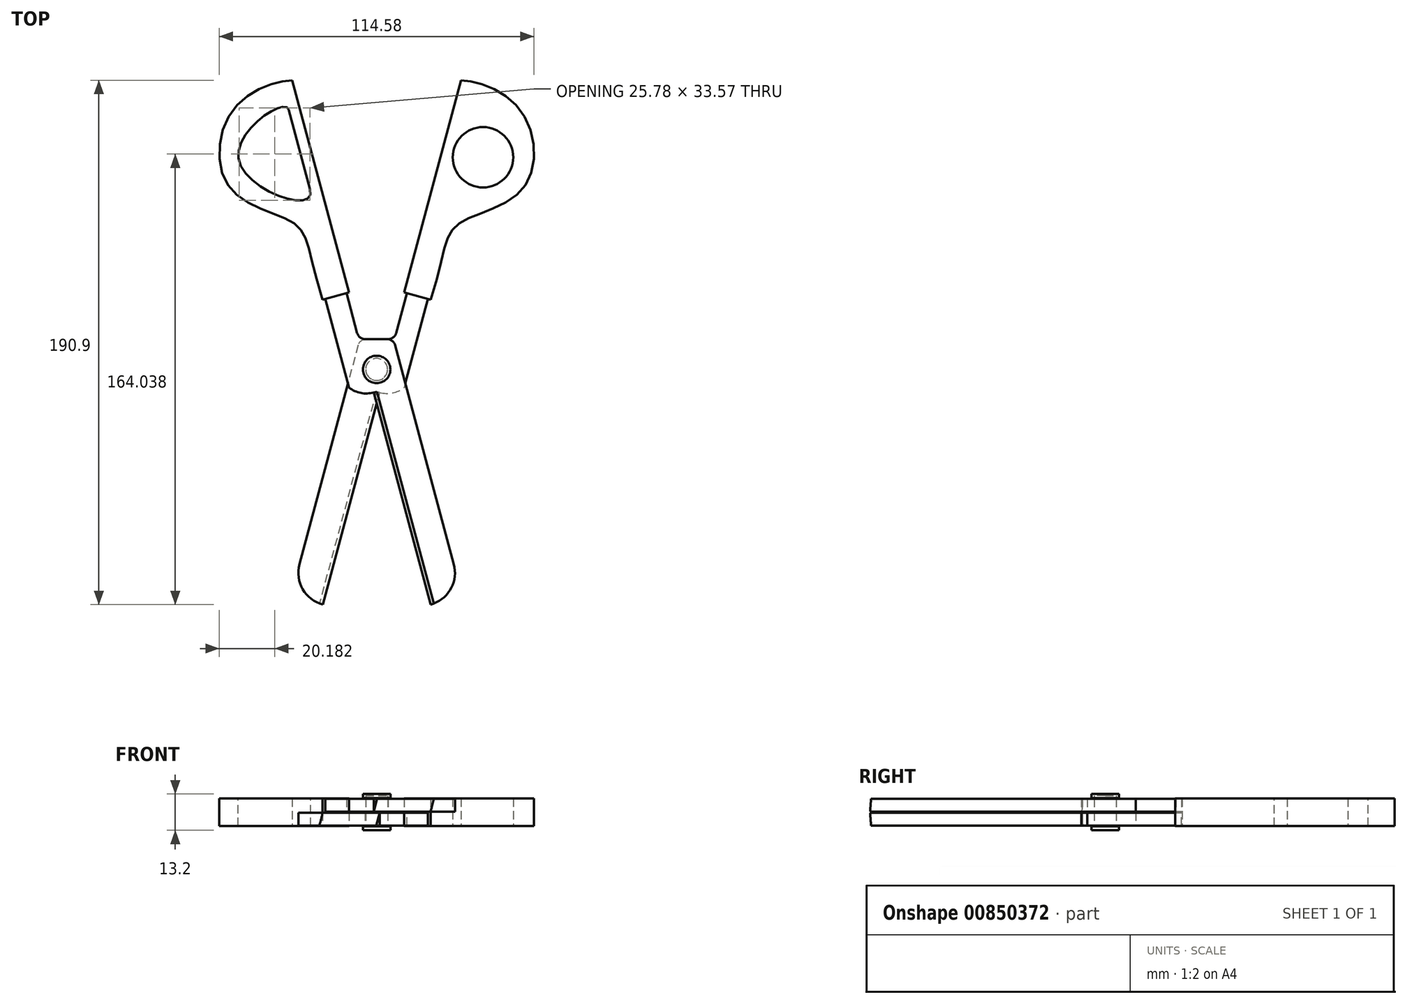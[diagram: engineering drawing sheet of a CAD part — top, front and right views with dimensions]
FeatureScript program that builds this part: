
annotation { "Feature Type Name" : "Feature", "Feature Type Description" : "" }
export const myFeature = defineFeature(function(context is Context, id is Id, definition is map)
    precondition{}
    {
        {
            var Q0;
            Q0=qCreatedBy(makeId("Top.planeOp"),FACE);
            var sketch = newSketch(context, id + "F0", { "sketchPlane" : qUnion([Q0])});
            skLineSegment(sketch, "E0", {"start": v(10, 10) * mm, "end": v(30.7, 87.27) * mm});
            skLineSegment(sketch, "E1", {"start": v(10, 10) * mm, "end": v(19.66, 7.41) * mm});
            skFitSpline(sketch, "E2", {"points": [v(19.66, 7.41) * mm, v(30.07, 35.15) * mm, v(53.27, 47.9) * mm, v(52.13, 76.77) * mm, v(30.7, 87.27) * mm], "startDerivative": vector(62.66, 194.88) * mm, "endDerivative": vector(-72.65, 2.28) * mm});
            skLineSegment(sketch, "E3.MirrorCS", {"start": v(-10, 10) * mm, "end": v(-30.7, 87.27) * mm});
            skFitSpline(sketch, "E4.MirrorCS", {"points": [v(-19.66, 7.41) * mm, v(-30.07, 35.15) * mm, v(-53.27, 47.9) * mm, v(-52.13, 76.77) * mm, v(-30.7, 87.27) * mm], "startDerivative": vector(-62.66, 194.88) * mm, "endDerivative": vector(72.65, 2.28) * mm});
            skLineSegment(sketch, "E5.MirrorCS", {"start": v(-10, 10) * mm, "end": v(-19.66, 7.41) * mm});
            skSolve(sketch);
        }
        {
            var Q0;
            Q0=qSketchRegion(id+"F0",true);
            extrude(context, id + "F1", {"entities" : qUnion([Q0]), "endBound" : BoundingType.SYMMETRIC, "depth" : 10 * mm, "offsetDistance" : 25 * mm});
        }
        {
            var Q0;
            Q0=qCreatedBy(makeId("Top.planeOp"),FACE);
            var sketch = newSketch(context, id + "F2", { "sketchPlane" : qUnion([Q0])});
            skLineSegment(sketch, "E6", {"start": v(-31.98, 76.58) * mm, "end": v(-24.22, 47.6) * mm});
            skFitSpline(sketch, "E7", {"points": [v(-31.98, 76.58) * mm, v(-50.17, 58.1) * mm, v(-24.22, 47.6) * mm], "startDerivative": vector(-7.92, 29.54) * mm, "endDerivative": vector(-15.24, 56.87) * mm});
            skSolve(sketch);
        }
        {
            var Q0;
            Q0=qSketchRegion(id+"F2",true);
            extrude(context, id + "F3", {"entities" : qUnion([Q0]), "operationType" : NewBodyOperationType.REMOVE, "endBound" : BoundingType.SYMMETRIC, "oppositeDirection" : true, "depth" : 40 * mm, "offsetDistance" : 25 * mm});
        }
        {
            var Q0;
            Q0=qCreatedBy(makeId("Top.planeOp"),FACE);
            var sketch = newSketch(context, id + "F4", { "sketchPlane" : qUnion([Q0])});
            skCircle(sketch, "E8", {"center": v(38.72, 59.24) * mm, "radius": 11 * mm});
            skSolve(sketch);
        }
        {
            var Q0;
            Q0=qSketchRegion(id+"F4",true);
            extrude(context, id + "F5", {"entities" : qUnion([Q0]), "operationType" : NewBodyOperationType.REMOVE, "endBound" : BoundingType.SYMMETRIC, "depth" : 40 * mm, "offsetDistance" : 25 * mm});
        }
        {
            var Q0;
            Q0=qCreatedBy(makeId("Top.planeOp"),FACE);
            var sketch = newSketch(context, id + "F6", { "sketchPlane" : qUnion([Q0])});
            skCircle(sketch, "E9", {"center": v(0, -18) * mm, "radius": 4 * mm});
            skSolve(sketch);
        }
        {
            var Q0;
            Q0=qSketchRegion(id+"F6",true);
            extrude(context, id + "F7", {"entities" : qUnion([Q0]), "endBound" : BoundingType.SYMMETRIC, "depth" : 12 * mm, "offsetDistance" : 25 * mm});
        }
        {
            var Q0;
            Q0=qCreatedBy(makeId("Top.planeOp"),FACE);
            cPlane(context, id + "F8", {"entities" : qUnion([Q0]), "cplaneType" : CPlaneType.OFFSET, "offset" : 2.5 * mm, "width" : 150 * mm, "height" : 150 * mm});
        }
        {
            var Q0;
            Q0=qCreatedBy(id+"F8.planeOp",FACE);
            var sketch = newSketch(context, id + "F9", { "sketchPlane" : qUnion([Q0])});
            skLineSegment(sketch, "E10", {"start": v(-19.99, 12.5) * mm, "end": v(-14.81, -6.82) * mm});
            skLineSegment(sketch, "E11", {"start": v(-12.26, 14.57) * mm, "end": v(-7.08, -4.75) * mm});
            skArc(sketch, "E12", {"start": v(-7.08, -4.75) * mm, "mid": v(-6.01, -6.35) * mm, "end": v(-4.19, -6.97) * mm});
            skLineSegment(sketch, "E13", {"start": v(-4.19, -6.97) * mm, "end": v(0, -6.97) * mm});
            skLineSegment(sketch, "E14.MirrorCS", {"start": v(4.19, -6.97) * mm, "end": v(0, -6.97) * mm});
            skArc(sketch, "E15", {"start": v(4.19, -6.97) * mm, "mid": v(5.8, -7.68) * mm, "end": v(6.73, -9.17) * mm});
            skLineSegment(sketch, "E16", {"start": v(6.73, -9.17) * mm, "end": v(28.1, -88.93) * mm});
            skLineSegment(sketch, "E17", {"start": v(-14.81, -6.82) * mm, "end": v(-10.04, -24.61) * mm});
            skArc(sketch, "E18", {"start": v(-10.04, -24.61) * mm, "mid": v(-5.78, -26.56) * mm, "end": v(-1.1, -26.35) * mm});
            skLineSegment(sketch, "E19", {"start": v(-1.1, -26.35) * mm, "end": v(19.61, -103.63) * mm});
            skArc(sketch, "E20", {"start": v(19.61, -103.63) * mm, "mid": v(26.9, -98.04) * mm, "end": v(28.1, -88.93) * mm});
            skLineSegment(sketch, "E21", {"start": v(-19.99, 12.5) * mm, "end": v(-12.26, 14.57) * mm});
            skSolve(sketch);
        }
        {
            var Q0;
            Q0=qSketchRegion(id+"F9",true);
            extrude(context, id + "F10", {"entities" : qUnion([Q0]), "endBound" : BoundingType.SYMMETRIC, "depth" : 4.7 * mm, "offsetDistance" : 25 * mm});
        }
        {
            var Q0;
            Q0=qCreatedBy(makeId("Top.planeOp"),FACE);
            cPlane(context, id + "F11", {"entities" : qUnion([Q0]), "cplaneType" : CPlaneType.OFFSET, "offset" : 2.5 * mm, "oppositeDirection" : true, "width" : 150 * mm, "height" : 150 * mm});
        }
        {
            var Q0;
            Q0=qCreatedBy(id+"F11.planeOp",FACE);
            var sketch = newSketch(context, id + "F12", { "sketchPlane" : qUnion([Q0])});
            skLineSegment(sketch, "E22", {"start": v(12.26, 14.57) * mm, "end": v(7.08, -4.75) * mm});
            skLineSegment(sketch, "E23", {"start": v(19.99, 12.5) * mm, "end": v(14.81, -6.82) * mm});
            skArc(sketch, "E24", {"start": v(7.08, -4.75) * mm, "mid": v(6.01, -6.35) * mm, "end": v(4.19, -6.97) * mm});
            skLineSegment(sketch, "E25", {"start": v(4.19, -6.97) * mm, "end": v(0, -6.97) * mm});
            skLineSegment(sketch, "E26.MirrorCS", {"start": v(-4.19, -6.97) * mm, "end": v(0, -6.97) * mm});
            skArc(sketch, "E27", {"start": v(-4.19, -6.97) * mm, "mid": v(-5.8, -7.68) * mm, "end": v(-6.73, -9.17) * mm});
            skLineSegment(sketch, "E28", {"start": v(-6.73, -9.17) * mm, "end": v(-28.1, -88.93) * mm});
            skLineSegment(sketch, "E29", {"start": v(14.81, -6.82) * mm, "end": v(10.04, -24.61) * mm});
            skArc(sketch, "E30", {"start": v(10.04, -24.61) * mm, "mid": v(5.78, -26.56) * mm, "end": v(1.1, -26.35) * mm});
            skLineSegment(sketch, "E31", {"start": v(1.1, -26.35) * mm, "end": v(-19.61, -103.63) * mm});
            skArc(sketch, "E32", {"start": v(-28.1, -88.93) * mm, "mid": v(-26.9, -98.04) * mm, "end": v(-19.61, -103.63) * mm});
            skLineSegment(sketch, "E33", {"start": v(12.26, 14.57) * mm, "end": v(19.99, 12.5) * mm});
            skSolve(sketch);
        }
        {
            var Q0;
            Q0=makeQuery(id+"F10.opExtrude","SWEPT_FACE",FACE,{"disambiguationData":[OSD([sQuery(id+"F9.wireOp",EDGE,"E21")])]});
            cPlane(context, id + "F13", {"entities" : qUnion([Q0]), "cplaneType" : CPlaneType.OFFSET, "offset" : 122.5 * mm, "oppositeDirection" : true, "width" : 150 * mm, "height" : 150 * mm});
        }
        {
            var Q0;
            Q0=qCreatedBy(id+"F13.planeOp",FACE);
            var sketch = newSketch(context, id + "F14", { "sketchPlane" : qUnion([Q0])});
            skLineSegment(sketch, "E34", {"start": v(7.88, 0.15) * mm, "end": v(6.62, 4.85) * mm});
            skLineSegment(sketch, "E35", {"start": v(6.62, 4.85) * mm, "end": v(7.88, 4.85) * mm});
            skLineSegment(sketch, "E36", {"start": v(7.88, 4.85) * mm, "end": v(7.88, 0.15) * mm});
            skSolve(sketch);
        }
        {
            var Q0;
            Q0=qSketchRegion(id+"F14",true);
            extrude(context, id + "F15", {"entities" : qUnion([Q0]), "operationType" : NewBodyOperationType.REMOVE, "depth" : 80 * mm, "offsetDistance" : 25 * mm});
        }
        {
            var Q0;
            Q0=qSketchRegion(id+"F12",true);
            extrude(context, id + "F16", {"entities" : qUnion([Q0]), "endBound" : BoundingType.SYMMETRIC, "depth" : 4.7 * mm, "offsetDistance" : 25 * mm});
        }
        {
            var Q0;
            Q0=makeQuery(id+"F10.opExtrude","CAP_FACE",FACE,{"disambiguationData":[OSD([sQuery(id+"F9.wireOp",EDGE,"E10"),sQuery(id+"F9.wireOp",EDGE,"E11"),sQuery(id+"F9.wireOp",EDGE,"E12"),sQuery(id+"F9.wireOp",EDGE,"E13"),sQuery(id+"F9.wireOp",EDGE,"E14.MirrorCS"),sQuery(id+"F9.wireOp",EDGE,"E15"),sQuery(id+"F9.wireOp",EDGE,"E16"),sQuery(id+"F9.wireOp",EDGE,"E17"),sQuery(id+"F9.wireOp",EDGE,"E18"),sQuery(id+"F9.wireOp",EDGE,"E19"),sQuery(id+"F9.wireOp",EDGE,"E20"),sQuery(id+"F9.wireOp",EDGE,"E21")])],"isStart":false});
            cPlane(context, id + "F17", {"entities" : qUnion([Q0]), "cplaneType" : CPlaneType.OFFSET, "offset" : 1 * mm, "width" : 150 * mm, "height" : 150 * mm});
        }
        {
            var Q0;
            Q0=qCreatedBy(id+"F17.planeOp",FACE);
            var sketch = newSketch(context, id + "F18", { "sketchPlane" : qUnion([Q0])});
            skCircle(sketch, "E37", {"center": v(0, -18) * mm, "radius": 5 * mm});
            skSolve(sketch);
        }
        {
            var Q0;
            Q0=qSketchRegion(id+"F18",true);
            extrude(context, id + "F19", {"entities" : qUnion([Q0]), "endBound" : BoundingType.SYMMETRIC, "depth" : 1.5 * mm, "offsetDistance" : 25 * mm});
        }
        {
            var Q0;
            Q0=makeQuery(id+"F16.opExtrude","SWEPT_FACE",FACE,{"disambiguationData":[OSD([sQuery(id+"F12.wireOp",EDGE,"E33")])]});
            cPlane(context, id + "F20", {"entities" : qUnion([Q0]), "cplaneType" : CPlaneType.OFFSET, "offset" : 122.5 * mm, "oppositeDirection" : true, "width" : 150 * mm, "height" : 150 * mm});
        }
        {
            var Q0;
            Q0=qCreatedBy(id+"F20.planeOp",FACE);
            var sketch = newSketch(context, id + "F21", { "sketchPlane" : qUnion([Q0])});
            skLineSegment(sketch, "E38", {"start": v(-7.88, -0.15) * mm, "end": v(-7.88, -4.85) * mm});
            skLineSegment(sketch, "E39", {"start": v(-7.88, -4.85) * mm, "end": v(-6.62, -4.85) * mm});
            skLineSegment(sketch, "E40", {"start": v(-6.62, -4.85) * mm, "end": v(-7.88, -0.15) * mm});
            skSolve(sketch);
        }
        {
            var Q0;
            Q0=qSketchRegion(id+"F21",true);
            extrude(context, id + "F22", {"entities" : qUnion([Q0]), "operationType" : NewBodyOperationType.REMOVE, "depth" : 80 * mm, "offsetDistance" : 25 * mm});
        }
        {
            var Q0;
            Q0=makeQuery(id+"F16.opExtrude","CAP_FACE",FACE,{"disambiguationData":[OSD([sQuery(id+"F12.wireOp",EDGE,"E22"),sQuery(id+"F12.wireOp",EDGE,"E23"),sQuery(id+"F12.wireOp",EDGE,"E24"),sQuery(id+"F12.wireOp",EDGE,"E25"),sQuery(id+"F12.wireOp",EDGE,"E26.MirrorCS"),sQuery(id+"F12.wireOp",EDGE,"E27"),sQuery(id+"F12.wireOp",EDGE,"E28"),sQuery(id+"F12.wireOp",EDGE,"E29"),sQuery(id+"F12.wireOp",EDGE,"E30"),sQuery(id+"F12.wireOp",EDGE,"E31"),sQuery(id+"F12.wireOp",EDGE,"E32"),sQuery(id+"F12.wireOp",EDGE,"E33")])],"isStart":true});
            cPlane(context, id + "F23", {"entities" : qUnion([Q0]), "cplaneType" : CPlaneType.OFFSET, "offset" : 1 * mm, "width" : 150 * mm, "height" : 150 * mm});
        }
        {
            var Q0;
            Q0=qCreatedBy(id+"F23.planeOp",FACE);
            var sketch = newSketch(context, id + "F24", { "sketchPlane" : qUnion([Q0])});
            skCircle(sketch, "E41", {"center": v(0, 18) * mm, "radius": 5 * mm});
            skSolve(sketch);
        }
        {
            var Q0;
            Q0=qSketchRegion(id+"F24",true);
            extrude(context, id + "F25", {"entities" : qUnion([Q0]), "operationType" : NewBodyOperationType.ADD, "endBound" : BoundingType.SYMMETRIC, "depth" : 1.5 * mm, "offsetDistance" : 25 * mm});
        }
        {
            var Q0;
            Q0=makeQuery(id+"F1.opExtrude","SWEPT_BODY",BODY,{"disambiguationData":[OSD([sQuery(id+"F0.wireOp",EDGE,"E0"),sQuery(id+"F0.wireOp",EDGE,"E1"),sQuery(id+"F0.wireOp",EDGE,"E2")])]});
            var Q1;
            Q1=makeQuery(id+"F16.opExtrude","SWEPT_BODY",BODY,{"disambiguationData":[OSD([sQuery(id+"F12.wireOp",EDGE,"E22"),sQuery(id+"F12.wireOp",EDGE,"E23"),sQuery(id+"F12.wireOp",EDGE,"E24"),sQuery(id+"F12.wireOp",EDGE,"E25"),sQuery(id+"F12.wireOp",EDGE,"E26.MirrorCS"),sQuery(id+"F12.wireOp",EDGE,"E27"),sQuery(id+"F12.wireOp",EDGE,"E28"),sQuery(id+"F12.wireOp",EDGE,"E29"),sQuery(id+"F12.wireOp",EDGE,"E30"),sQuery(id+"F12.wireOp",EDGE,"E31"),sQuery(id+"F12.wireOp",EDGE,"E32"),sQuery(id+"F12.wireOp",EDGE,"E33")])]});
            booleanBodies(context, id + "F26", {"operationType" : BooleanOperationType.SUBTRACTION, "tools" : qUnion([Q0]), "targets" : qUnion([Q1]), "keepTools" : true});
        }
        {
            var Q0;
            Q0=makeQuery(id+"F1.opExtrude","SWEPT_BODY",BODY,{"disambiguationData":[OSD([sQuery(id+"F0.wireOp",EDGE,"E3.MirrorCS"),sQuery(id+"F0.wireOp",EDGE,"E4.MirrorCS"),sQuery(id+"F0.wireOp",EDGE,"E5.MirrorCS")])]});
            var Q1;
            Q1=makeQuery(id+"F10.opExtrude","SWEPT_BODY",BODY,{"disambiguationData":[OSD([sQuery(id+"F9.wireOp",EDGE,"E10"),sQuery(id+"F9.wireOp",EDGE,"E11"),sQuery(id+"F9.wireOp",EDGE,"E12"),sQuery(id+"F9.wireOp",EDGE,"E13"),sQuery(id+"F9.wireOp",EDGE,"E14.MirrorCS"),sQuery(id+"F9.wireOp",EDGE,"E15"),sQuery(id+"F9.wireOp",EDGE,"E16"),sQuery(id+"F9.wireOp",EDGE,"E17"),sQuery(id+"F9.wireOp",EDGE,"E18"),sQuery(id+"F9.wireOp",EDGE,"E19"),sQuery(id+"F9.wireOp",EDGE,"E20"),sQuery(id+"F9.wireOp",EDGE,"E21")])]});
            booleanBodies(context, id + "F27", {"operationType" : BooleanOperationType.SUBTRACTION, "tools" : qUnion([Q0]), "targets" : qUnion([Q1]), "keepTools" : true});
        }
        {
            var Q0;
            Q0=makeQuery(id+"F7.opExtrude","SWEPT_BODY",BODY,{"disambiguationData":[OSD([sQuery(id+"F6.wireOp",EDGE,"E9")])]});
            var Q1;
            Q1=makeQuery(id+"F16.opExtrude","SWEPT_BODY",BODY,{"disambiguationData":[OSD([sQuery(id+"F12.wireOp",EDGE,"E22"),sQuery(id+"F12.wireOp",EDGE,"E23"),sQuery(id+"F12.wireOp",EDGE,"E24"),sQuery(id+"F12.wireOp",EDGE,"E25"),sQuery(id+"F12.wireOp",EDGE,"E26.MirrorCS"),sQuery(id+"F12.wireOp",EDGE,"E27"),sQuery(id+"F12.wireOp",EDGE,"E28"),sQuery(id+"F12.wireOp",EDGE,"E29"),sQuery(id+"F12.wireOp",EDGE,"E30"),sQuery(id+"F12.wireOp",EDGE,"E31"),sQuery(id+"F12.wireOp",EDGE,"E32"),sQuery(id+"F12.wireOp",EDGE,"E33")])]});
            var Q2;
            Q2=makeQuery(id+"F10.opExtrude","SWEPT_BODY",BODY,{"disambiguationData":[OSD([sQuery(id+"F9.wireOp",EDGE,"E10"),sQuery(id+"F9.wireOp",EDGE,"E11"),sQuery(id+"F9.wireOp",EDGE,"E12"),sQuery(id+"F9.wireOp",EDGE,"E13"),sQuery(id+"F9.wireOp",EDGE,"E14.MirrorCS"),sQuery(id+"F9.wireOp",EDGE,"E15"),sQuery(id+"F9.wireOp",EDGE,"E16"),sQuery(id+"F9.wireOp",EDGE,"E17"),sQuery(id+"F9.wireOp",EDGE,"E18"),sQuery(id+"F9.wireOp",EDGE,"E19"),sQuery(id+"F9.wireOp",EDGE,"E20"),sQuery(id+"F9.wireOp",EDGE,"E21")])]});
            booleanBodies(context, id + "F28", {"operationType" : BooleanOperationType.SUBTRACTION, "tools" : qUnion([Q0]), "targets" : qUnion([Q1, Q2]), "keepTools" : true});
        }
    });
